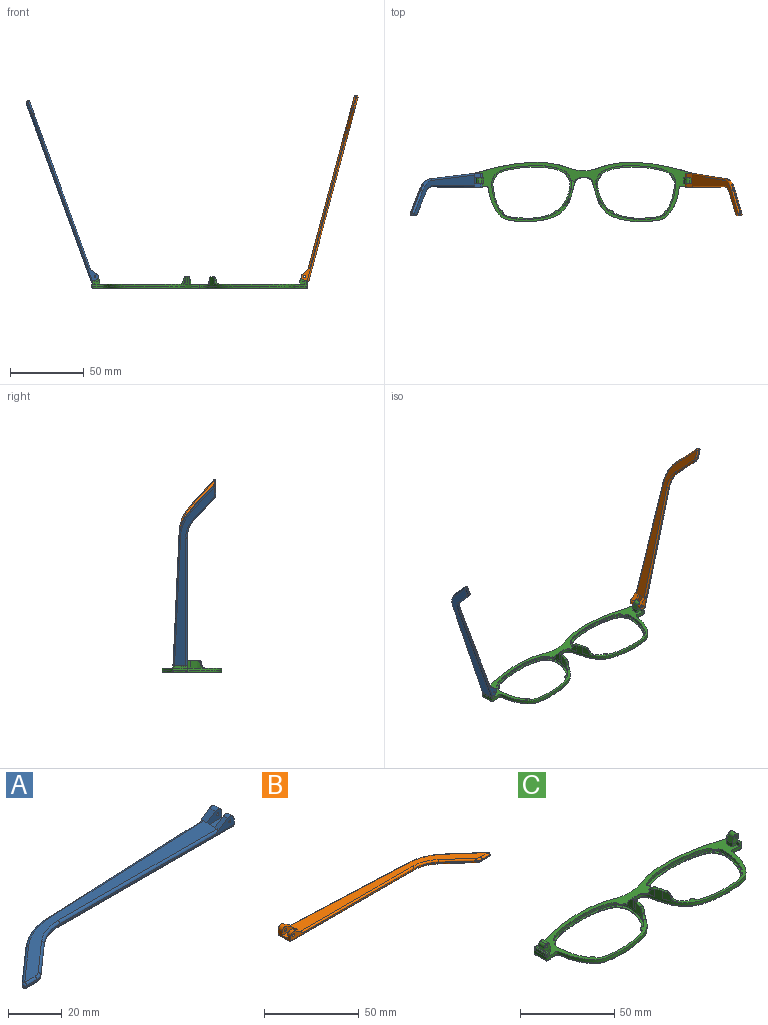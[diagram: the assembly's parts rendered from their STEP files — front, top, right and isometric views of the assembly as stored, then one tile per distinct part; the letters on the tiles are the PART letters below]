
ASSEMBLY  parts=3 mates=2
PART A: 43 faces, bbox 130.2x29.5x5.9 mm
  f0: plane 9.62x3.72mm, normal (1,0,0), area 24.7mm2, adj f1,f3,f4,f5,f10,f16,f18,f28
  f1: cylinder r=2.2mm len=3.45mm, axis (0,-1,0), area 11mm2, adj f0,f2,f4,f37
  f2: plane 6.01x3.91mm, normal (-0.55,0,0.84), area 12.7mm2, adj f1,f4,f9,f19,f37
  f3: plane 2.26x0.1mm, normal (0,0,1), area 0.1mm2, adj f0,f5,f18
  f4: plane 92.1x4.9mm, normal (0,-1,0), area 79.9mm2, adj f0,f1,f2,f14,f19,f36,f42
  f5: plane 93.42x4.13mm, normal (-0.04,1,0), area 64.8mm2, adj f0,f3,f11,f15,f17,f27,f28
  f6: plane 17.82x15.72mm, normal (-0.66,0.75,0), area 14.3mm2, adj f11,f12,f25,f30
  f7: plane 5.46x0.6mm, normal (0,-1,0), area 3.3mm2, adj f12,f13,f23,f32
  f8: plane 14.99x13.23mm, normal (0.66,-0.75,0), area 12mm2, adj f13,f14,f21,f34
  f9: plane 121.18x26.73mm, normal (0,0,1), area 627.7mm2, adj f2,f17,f19,f20,f21,f22,f23,f25
  f10: plane 129.1x27.08mm, normal (0,0,-1), area 686.5mm2, adj f0,f28,f29,f30,f32,f33,f34,f35
  f11: cylinder r=30mm len=18.52mm, axis (0,0,-1), area 12.2mm2, adj f5,f6,f26,f29
  f12: cylinder r=1mm len=1.75mm, axis (0,0,-1), area 1.5mm2, adj f6,f7,f24,f31
  f13: cylinder r=5mm len=3.31mm, axis (0,0,-1), area 2.2mm2, adj f7,f8,f22,f33
  f14: cylinder r=20mm len=13.23mm, axis (0,0,1), area 8.7mm2, adj f4,f8,f20,f35
  f15: plane 5.66x0.25mm, normal (0,0,-1), area 0.7mm2, adj f5,f17,f18
  f16: cylinder r=2.2mm len=3.45mm, axis (0,-1,0), area 14.8mm2, adj f0,f17,f18,f38
  f17: plane 6.01x3.91mm, normal (-0.55,0,0.84), area 16.9mm2, adj f5,f9,f15,f16,f18,f27,f38
  f18: plane 7.92x3.3mm, normal (0,1,0), area 15.9mm2, adj f0,f3,f15,f16,f17,f41
  f19: cylinder r=1mm len=84.18mm, axis (-1,0,0), area 131.4mm2, adj f2,f4,f9,f20
  f20: torus R=21mm, axis (0,0,1), area 23.1mm2, adj f9,f14,f19,f21
  f21: cylinder r=1mm len=15.65mm, axis (-0.75,-0.66,0), area 31.4mm2, adj f8,f9,f20,f22
  f22: torus R=4mm, axis (0,0,1), area 5.3mm2, adj f9,f13,f21,f23
  f23: cylinder r=1mm len=5.46mm, axis (-1,0,0), area 8.6mm2, adj f7,f9,f22,f24
  f24: sphere r=1mm, area 2.4mm2, adj f12,f23,f25
  f25: cylinder r=1mm len=18.48mm, axis (0.75,0.66,0), area 37.3mm2, adj f6,f9,f24,f26
  f26: torus R=29mm, axis (0,0,1), area 31.6mm2, adj f9,f11,f25,f27
  f27: cylinder r=1mm len=85.5mm, axis (1,0.04,0), area 133.5mm2, adj f5,f9,f17,f26
  f28: cylinder r=1mm len=93.46mm, axis (-1,-0.04,0), area 146.9mm2, adj f0,f5,f10,f29
  f29: torus R=29mm, axis (0,0,1), area 31.6mm2, adj f10,f11,f28,f30
  f30: cylinder r=1mm len=18.48mm, axis (-0.75,-0.66,0), area 37.3mm2, adj f6,f10,f29,f31
  f31: sphere r=1mm, area 2.4mm2, adj f12,f30,f32
  f32: cylinder r=1mm len=5.46mm, axis (1,0,0), area 8.6mm2, adj f7,f10,f31,f33
  f33: torus R=4mm, axis (0,0,1), area 5.3mm2, adj f10,f13,f32,f34
  f34: cylinder r=1mm len=15.65mm, axis (0.75,0.66,0), area 31.4mm2, adj f8,f10,f33,f35
  f35: torus R=21mm, axis (0,0,1), area 23.1mm2, adj f10,f14,f34,f36
  f36: cylinder r=1mm len=92.1mm, axis (1,0,0), area 144.7mm2, adj f0,f4,f10,f35
  f37: plane 7.92x4.7mm, normal (0,1,0), area 27mm2, adj f0,f1,f2,f39,f40,f42
  f38: plane 7.92x4.7mm, normal (0,-1,0), area 27mm2, adj f0,f16,f17,f39,f40,f41
  f39: plane 7.92x4.1mm, normal (0,0,1), area 32.5mm2, adj f0,f37,f38,f40
  f40: plane 4.1x1.4mm, normal (1,0,0), area 5.7mm2, adj f9,f37,f38,f39
  f41: cylinder r=0.5mm len=3.1mm, axis (0,-1,0), area 9.7mm2, adj f18,f38
  f42: cylinder r=0.5mm len=2.3mm, axis (0,-1,0), area 7.2mm2, adj f4,f37
PART B: 43 faces, bbox 130.2x29.5x5.9 mm
  f0: plane 9.62x3.72mm, normal (-1,0,0), area 24.7mm2, adj f1,f3,f4,f5,f10,f16,f18,f28
  f1: cylinder r=2.2mm len=3.45mm, axis (0,-1,0), area 11mm2, adj f0,f2,f4,f37
  f2: plane 6.01x3.91mm, normal (0.55,0,0.84), area 12.7mm2, adj f1,f4,f9,f19,f37
  f3: plane 2.26x0.1mm, normal (0,0,1), area 0.1mm2, adj f0,f5,f18
  f4: plane 92.1x4.9mm, normal (0,-1,0), area 78.2mm2, adj f0,f1,f2,f14,f19,f36,f42
  f5: plane 93.42x4.13mm, normal (0.04,1,0), area 64.8mm2, adj f0,f3,f11,f15,f17,f27,f28
  f6: plane 17.82x15.72mm, normal (0.66,0.75,0), area 14.3mm2, adj f11,f12,f25,f30
  f7: plane 5.46x0.6mm, normal (0,-1,0), area 3.3mm2, adj f12,f13,f23,f32
  f8: plane 14.99x13.23mm, normal (-0.66,-0.75,0), area 12mm2, adj f13,f14,f21,f34
  f9: plane 121.18x26.73mm, normal (0,0,1), area 627.7mm2, adj f2,f17,f19,f20,f21,f22,f23,f25
  f10: plane 129.1x27.08mm, normal (0,0,-1), area 686.5mm2, adj f0,f28,f29,f30,f32,f33,f34,f35
  f11: cylinder r=30mm len=18.52mm, axis (0,0,-1), area 12.2mm2, adj f5,f6,f26,f29
  f12: cylinder r=1mm len=1.75mm, axis (0,0,-1), area 1.5mm2, adj f6,f7,f24,f31
  f13: cylinder r=5mm len=3.31mm, axis (0,0,-1), area 2.2mm2, adj f7,f8,f22,f33
  f14: cylinder r=20mm len=13.23mm, axis (0,0,1), area 8.7mm2, adj f4,f8,f20,f35
  f15: plane 5.66x0.25mm, normal (0,0,-1), area 0.7mm2, adj f5,f17,f18
  f16: cylinder r=2.2mm len=3.45mm, axis (0,-1,0), area 14.8mm2, adj f0,f17,f18,f38
  f17: plane 6.01x3.91mm, normal (0.55,0,0.84), area 16.9mm2, adj f5,f9,f15,f16,f18,f27,f38
  f18: plane 7.92x3.3mm, normal (0,1,0), area 14.3mm2, adj f0,f3,f15,f16,f17,f41
  f19: cylinder r=1mm len=84.18mm, axis (1,0,0), area 131.4mm2, adj f2,f4,f9,f20
  f20: torus R=21mm, axis (0,0,1), area 23.1mm2, adj f9,f14,f19,f21
  f21: cylinder r=1mm len=15.65mm, axis (0.75,-0.66,0), area 31.4mm2, adj f8,f9,f20,f22
  f22: torus R=4mm, axis (0,0,1), area 5.3mm2, adj f9,f13,f21,f23
  f23: cylinder r=1mm len=5.46mm, axis (1,0,0), area 8.6mm2, adj f7,f9,f22,f24
  f24: sphere r=1mm, area 2.4mm2, adj f12,f23,f25
  f25: cylinder r=1mm len=18.48mm, axis (-0.75,0.66,0), area 37.3mm2, adj f6,f9,f24,f26
  f26: torus R=29mm, axis (0,0,1), area 31.6mm2, adj f9,f11,f25,f27
  f27: cylinder r=1mm len=85.5mm, axis (-1,0.04,0), area 133.5mm2, adj f5,f9,f17,f26
  f28: cylinder r=1mm len=93.46mm, axis (1,-0.04,0), area 146.9mm2, adj f0,f5,f10,f29
  f29: torus R=29mm, axis (0,0,1), area 31.6mm2, adj f10,f11,f28,f30
  f30: cylinder r=1mm len=18.48mm, axis (0.75,-0.66,0), area 37.3mm2, adj f6,f10,f29,f31
  f31: sphere r=1mm, area 2.4mm2, adj f12,f30,f32
  f32: cylinder r=1mm len=5.46mm, axis (-1,0,0), area 8.6mm2, adj f7,f10,f31,f33
  f33: torus R=4mm, axis (0,0,1), area 5.3mm2, adj f10,f13,f32,f34
  f34: cylinder r=1mm len=15.65mm, axis (-0.75,0.66,0), area 31.4mm2, adj f8,f10,f33,f35
  f35: torus R=21mm, axis (0,0,1), area 23.1mm2, adj f10,f14,f34,f36
  f36: cylinder r=1mm len=92.1mm, axis (-1,0,0), area 144.7mm2, adj f0,f4,f10,f35
  f37: plane 7.92x4.7mm, normal (0,1,0), area 25.4mm2, adj f0,f1,f2,f39,f40,f42
  f38: plane 7.92x4.7mm, normal (0,-1,0), area 25.4mm2, adj f0,f16,f17,f39,f40,f41
  f39: plane 7.92x4.1mm, normal (0,0,1), area 32.5mm2, adj f0,f37,f38,f40
  f40: plane 4.1x1.4mm, normal (-1,0,0), area 5.7mm2, adj f9,f37,f38,f39
  f41: cylinder r=0.88mm len=3.1mm, axis (0,-1,0), area 17mm2, adj f18,f38
  f42: cylinder r=0.88mm len=2.3mm, axis (0,-1,0), area 12.6mm2, adj f4,f37
PART C: 118 faces, bbox 147.4x41.1x17.6 mm
  f0: plane 2.18x0.47mm, normal (0,0,1), area 0mm2, adj f1,f117
  f1: extruded ~5x2.15mm, area 11mm2, adj f0,f2,f116,f117
  f2: plane 7.29x2.54mm, normal (0,0,1), area 7.9mm2, adj f1,f3,f111,f113,f116,f117
  f3: bspline ~7.27x7.27mm, area 5.8mm2, adj f2,f4,f111,f117
  f4: bspline ~3.56x3.3mm, area 6.1mm2, adj f3,f5,f111,f113,f117
  f5: plane 147.24x40.52mm, normal (0,0,1), area 859.6mm2, adj f4,f6,f26,f27,f28,f29,f30,f31
  f6: plane 4.57x1.81mm, normal (1,0,0), area 8.2mm2, adj f5,f7,f8,f26
  f7: cylinder r=1mm len=1.81mm, axis (0,0,-1), area 0mm2, adj f6,f113
  f8: plane 5.67x0.93mm, normal (0.34,0,0.94), area 4.5mm2, adj f6,f9,f17,f26
  f9: bspline ~1.56x0.8mm, area 1.3mm2, adj f8,f10,f17,f113
  f10: plane 2.62x0.92mm, normal (0.34,0,0.94), area 1.9mm2, adj f9,f11,f14,f16,f17
  f11: plane 2.1x1.33mm, normal (0,-1,0), area 2.8mm2, adj f10,f12,f16,f17,f32
  f12: plane 1.34x0.06mm, normal (0,0,1), area 0mm2, adj f11,f13,f113
  f13: plane 2.66x1.15mm, normal (0,0,1), area 0.2mm2, adj f12,f14,f16,f113
  f14: plane 1.81x1.55mm, normal (1,0,0), area 2.8mm2, adj f10,f13,f15,f16
  f15: cylinder r=1mm len=1.81mm, axis (0,0,-1), area 0mm2, adj f14,f113
  f16: cylinder r=1mm len=2.07mm, axis (0,0,-1), area 2.5mm2, adj f10,f11,f13,f14
  f17: plane 9.6x1.25mm, normal (0,0,1), area 8.1mm2, adj f8,f9,f10,f11,f18,f25,f26,f27
  f18: plane 5.77x5.06mm, normal (0,-1,0), area 17mm2, adj f17,f19,f20,f22,f23,f24,f25,f31
  f19: cylinder r=1.98mm len=4mm, axis (0,-1,0), area 12.4mm2, adj f18,f23,f25,f29
  f20: plane 4x3.31mm, normal (-0.94,0,0.34), area 14.1mm2, adj f18,f21,f22,f29
  f21: plane 4x0.02mm, normal (0.34,0,0.94), area 0.1mm2, adj f20,f29,f30
  f22: cylinder r=1.98mm len=4mm, axis (0,1,0), area 12.4mm2, adj f18,f20,f23,f29
  f23: plane 4x0.01mm, normal (0.34,0,0.94), area 0mm2, adj f18,f19,f22,f29
  f24: cylinder r=0.88mm len=4mm, axis (0,-1,0), area 22mm2, adj f18,f29
  f25: plane 4x2.21mm, normal (0.94,0,-0.34), area 9.4mm2, adj f17,f18,f19,f29
  f26: cylinder r=1mm len=2.1mm, axis (0,0,1), area 3.1mm2, adj f5,f6,f8,f17,f27
  f27: plane 2.1x1.04mm, normal (0,1,0), area 2.2mm2, adj f5,f17,f26,f28
  f28: plane 3.3x2.1mm, normal (-1,0,0), area 6.9mm2, adj f5,f17,f27,f29
  f29: plane 6.97x5.07mm, normal (0,1,0), area 22.7mm2, adj f5,f17,f19,f20,f21,f22,f23,f24
  f30: plane 4x2.36mm, normal (-1,0,0), area 9.5mm2, adj f5,f21,f29,f31
  f31: plane 3.21x2.36mm, normal (0,-1,0), area 5.7mm2, adj f5,f18,f30,f32
  f32: plane 2.3x2.1mm, normal (-1,0,0), area 4.8mm2, adj f5,f11,f17,f18,f31
  f33: cylinder r=1.6mm len=2.84mm, axis (0,0,1), area 2.4mm2, adj f5,f34,f117
  f34: plane 2.85x2.41mm, normal (0,0,-1), area 3.7mm2, adj f33,f117
  f35: cylinder r=1.6mm len=2.73mm, axis (0,0,1), area 2.4mm2, adj f5,f36,f117
  f36: plane 2.74x2.56mm, normal (0,0,-1), area 3.9mm2, adj f35,f117
  f37: cylinder r=2.28mm len=3.25mm, axis (0,0,1), area 2.4mm2, adj f5,f38,f117
  f38: plane 3.26x2.59mm, normal (0,0,-1), area 4.2mm2, adj f37,f117
  f39: cylinder r=2.28mm len=3.65mm, axis (0,0,1), area 2.7mm2, adj f5,f40,f117
  f40: plane 3.67x2.67mm, normal (0,0,-1), area 5.4mm2, adj f39,f117
  f41: bspline ~7.26x3.96mm, area 3.3mm2, adj f5,f42,f113,f116
  f42: bspline ~7.26x3.96mm, area 3.3mm2, adj f5,f41,f43,f108
  f43: bspline ~15.47x15.31mm, area 17.7mm2, adj f5,f42,f44,f46,f50,f60,f108
  f44: extruded ~5x2.15mm, area 11mm2, adj f43,f45,f46,f60
  f45: plane 2.18x0.47mm, normal (0,0,1), area 0mm2, adj f44,f60
  f46: plane 7.29x2.54mm, normal (0,0,1), area 7.9mm2, adj f43,f44,f47,f49,f60,f108
  f47: extruded ~5x4.6mm, area 23.2mm2, adj f46,f48,f49,f80,f108
  f48: plane 4.66x1.62mm, normal (0,0,1), area 0.3mm2, adj f47,f108
  f49: bspline ~7.27x7.27mm, area 5.8mm2, adj f46,f47,f60,f80
  f50: extruded ~4.87x3.66mm, area 11.4mm2, adj f43,f51,f108
  f51: bspline ~5.24x1.76mm, area 0mm2, adj f50,f108
  f52: cylinder r=2.28mm len=3.65mm, axis (0,0,1), area 2.7mm2, adj f5,f53,f60
  f53: plane 3.67x2.67mm, normal (0,0,-1), area 5.4mm2, adj f52,f60
  f54: cylinder r=2.28mm len=3.25mm, axis (0,0,1), area 2.4mm2, adj f5,f55,f60
  f55: plane 3.26x2.59mm, normal (0,0,-1), area 4.2mm2, adj f54,f60
  f56: cylinder r=1.6mm len=2.73mm, axis (0,0,1), area 2.4mm2, adj f5,f57,f60
  f57: plane 2.74x2.56mm, normal (0,0,-1), area 3.9mm2, adj f56,f60
  f58: cylinder r=1.6mm len=2.84mm, axis (0,0,1), area 2.4mm2, adj f5,f59,f60
  f59: plane 2.85x2.41mm, normal (0,0,-1), area 3.7mm2, adj f58,f60
  f60: extruded ~54.04x36.54mm, area 199.7mm2, adj f5,f43,f44,f45,f46,f49,f52,f53
  f61: extruded ~54.04x36.54mm, area 153.6mm2, adj f60,f62
  f62: plane 54.33x36.74mm, normal (0,0,1), area 147mm2, adj f61,f63
  f63: bspline ~54.19x36.75mm, area 228.1mm2, adj f62,f64
  f64: plane 144.78x38.29mm, normal (0,0,-1), area 582.7mm2, adj f63,f65,f68,f69,f70,f71,f73,f75
  f65: bspline ~10.36x1.38mm, area 12.6mm2, adj f64,f66,f67,f113
  f66: bspline ~1.01x1mm, area 0.9mm2, adj f65,f76,f113
  f67: bspline ~1.04x1mm, area 0.7mm2, adj f65,f68,f113
  f68: bspline ~45.54x8.54mm, area 59.8mm2, adj f64,f67,f69,f113
  f69: bspline ~37.06x6.7mm, area 56.6mm2, adj f64,f68,f70,f110
  f70: bspline ~37.06x6.7mm, area 56.6mm2, adj f64,f69,f71,f109
  f71: bspline ~45.54x8.54mm, area 59.8mm2, adj f64,f70,f72,f108
  f72: bspline ~1.04x1mm, area 0.8mm2, adj f71,f73,f108
  f73: bspline ~10.36x1.38mm, area 12.6mm2, adj f64,f72,f74,f108
  f74: bspline ~1.01x1mm, area 1mm2, adj f73,f75,f108
  f75: bspline ~75.28x30.82mm, area 161.5mm2, adj f64,f74,f76,f108
  f76: bspline ~75.28x30.82mm, area 161.5mm2, adj f64,f66,f75,f113
  f77: bspline ~54.19x36.75mm, area 228.1mm2, adj f64,f78
  f78: plane 54.33x36.74mm, normal (0,0,1), area 147mm2, adj f77,f79
  f79: extruded ~54.04x36.54mm, area 153.6mm2, adj f78,f117
  f80: bspline ~3.56x3.3mm, area 6.1mm2, adj f5,f47,f49,f60,f108
  f81: plane 2.3x2.1mm, normal (1,0,0), area 4.8mm2, adj f5,f82,f91,f98,f100
  f82: plane 2.1x1.33mm, normal (0,-1,0), area 2.8mm2, adj f81,f83,f89,f90,f91
  f83: plane 2.62x0.92mm, normal (-0.34,0,0.94), area 1.9mm2, adj f82,f84,f87,f90,f91
  f84: plane 1.81x1.55mm, normal (-1,0,0), area 2.8mm2, adj f83,f85,f86,f90
  f85: plane 2.66x1.15mm, normal (0,0,1), area 0.2mm2, adj f84,f89,f90,f108
  f86: cylinder r=1mm len=1.81mm, axis (0,0,-1), area 0mm2, adj f84,f108
  f87: bspline ~1.56x0.8mm, area 1.3mm2, adj f83,f88,f91,f108
  f88: plane 5.67x0.93mm, normal (-0.34,0,0.94), area 4.5mm2, adj f87,f91,f105,f106
  f89: plane 1.34x0.06mm, normal (0,0,1), area 0mm2, adj f82,f85,f108
  f90: cylinder r=1mm len=2.07mm, axis (0,0,-1), area 2.5mm2, adj f82,f83,f84,f85
  f91: plane 9.6x1.25mm, normal (0,0,1), area 8.1mm2, adj f81,f82,f83,f87,f88,f92,f98,f102
  f92: plane 4x2.21mm, normal (-0.94,0,-0.34), area 9.4mm2, adj f91,f93,f98,f102
  f93: cylinder r=1.98mm len=4mm, axis (0,-1,0), area 12.4mm2, adj f92,f94,f98,f102
  f94: plane 4x0.01mm, normal (-0.34,0,0.94), area 0mm2, adj f93,f95,f98,f102
  f95: cylinder r=1.98mm len=4mm, axis (0,1,0), area 12.4mm2, adj f94,f96,f98,f102
  f96: plane 4x3.31mm, normal (0.94,0,0.34), area 14.1mm2, adj f95,f97,f98,f102
  f97: plane 4x0.02mm, normal (-0.34,0,0.94), area 0.1mm2, adj f96,f101,f102
  f98: plane 5.77x5.06mm, normal (0,-1,0), area 17mm2, adj f81,f91,f92,f93,f94,f95,f96,f99
  f99: cylinder r=0.88mm len=4mm, axis (0,-1,0), area 22mm2, adj f98,f102
  f100: plane 3.21x2.36mm, normal (0,-1,0), area 5.7mm2, adj f5,f81,f98,f101
  f101: plane 4x2.36mm, normal (1,0,0), area 9.5mm2, adj f5,f97,f100,f102
  f102: plane 6.97x5.07mm, normal (0,1,0), area 22.7mm2, adj f5,f91,f92,f93,f94,f95,f96,f97
  f103: plane 3.3x2.1mm, normal (1,0,0), area 6.9mm2, adj f5,f91,f102,f104
  f104: plane 2.1x1.04mm, normal (0,1,0), area 2.2mm2, adj f5,f91,f103,f105
  f105: cylinder r=1mm len=2.1mm, axis (0,0,1), area 3.1mm2, adj f5,f88,f91,f104,f106
  f106: plane 4.57x1.81mm, normal (-1,0,0), area 8.2mm2, adj f5,f88,f105,f107
  f107: cylinder r=1mm len=1.81mm, axis (0,0,-1), area 0mm2, adj f106,f108
  f108: extruded ~73.25x40.28mm, area 293.5mm2, adj f5,f42,f43,f46,f47,f48,f50,f51
  f109: extruded ~35.39x5.69mm, area 72.2mm2, adj f5,f70,f108,f110
  f110: extruded ~35.39x5.69mm, area 72.2mm2, adj f5,f69,f109,f113
  f111: extruded ~5x4.6mm, area 23.2mm2, adj f2,f3,f4,f112,f113
  f112: plane 4.66x1.62mm, normal (0,0,1), area 0.3mm2, adj f111,f113
  f113: extruded ~73.25x40.28mm, area 293.5mm2, adj f2,f4,f5,f7,f9,f12,f13,f15
  f114: bspline ~5.24x1.76mm, area 0mm2, adj f113,f115
  f115: extruded ~4.87x3.66mm, area 12.7mm2, adj f113,f114,f116
  f116: bspline ~15.47x15.31mm, area 17.7mm2, adj f1,f2,f5,f41,f113,f115,f117
  f117: extruded ~54.04x36.54mm, area 199.7mm2, adj f0,f1,f2,f3,f4,f5,f33,f34
PLACE A rot(axis=(0,1,0),70deg) t=(-84.77,-5.75,56)mm
PLACE B rot(axis=(0,-1,0),75deg) t=(68.2,-5.75,-61.61)mm
PLACE C t=(10.15,-1.13,-5.77)mm
MATE revolute A.f1 <-> C.f95  axis (0,-1,0) through (-60.89,2.72,1.22)mm
MATE revolute B.f41 <-> C.f19  axis (0,-1,0) through (81.2,2.72,1.21)mm
